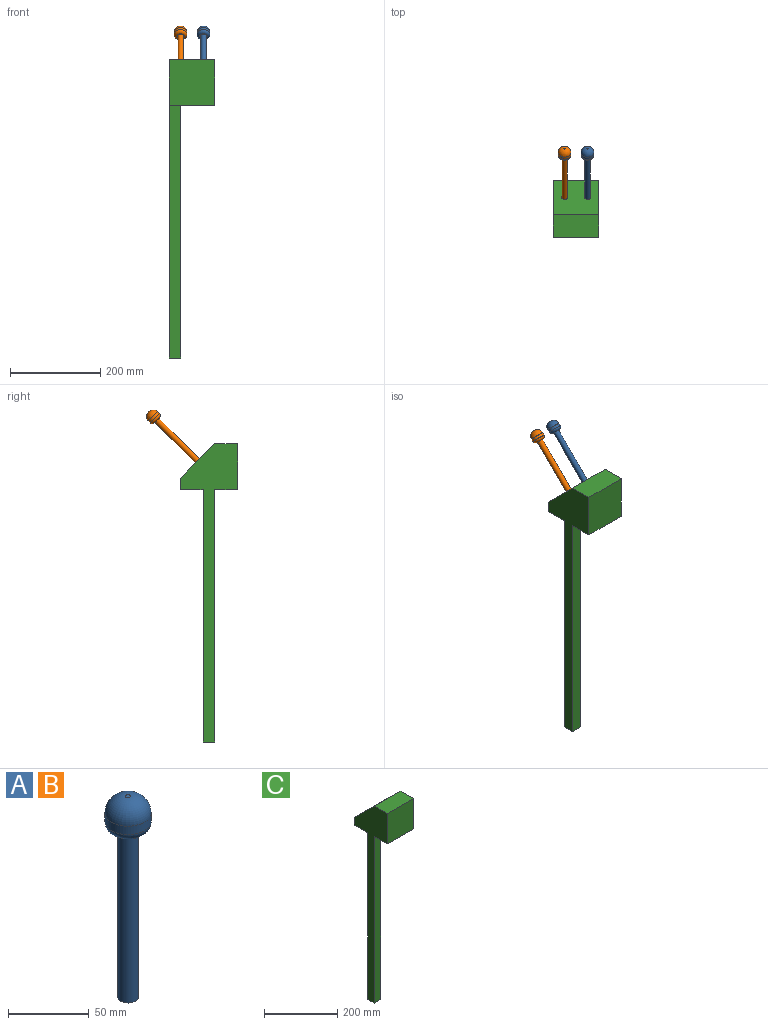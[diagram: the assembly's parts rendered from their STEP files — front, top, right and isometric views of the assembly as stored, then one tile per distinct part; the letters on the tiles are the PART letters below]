
ASSEMBLY  parts=3 mates=2
PART A: 7 faces, bbox 30.9x30.9x152.4 mm
  f0: cylinder r=6.35mm len=127mm, axis (0,0,-1), area 5067.1mm2, adj f1,f3
  f1: plane 12.7x12.7mm, normal (0,0,-1), area 126.7mm2, adj f0
  f2: cylinder r=14.29mm len=28.58mm, axis (0,0,-1), area 570mm2, adj f5,f6
  f3: plane 15.88x15.88mm, normal (0,0,-1), area 71.3mm2, adj f0,f6
  f4: plane 3.18x3.18mm, normal (0,0,1), area 7.9mm2, adj f5
  f5: torus R=1.59mm, axis (0,0,1), area 1212.4mm2, adj f2,f4
  f6: torus R=7.94mm, axis (0,0,1), area 750.8mm2, adj f2,f3
PART B: same geometry as A
PART C: 11 faces, bbox 101.6x127x660.4 mm
  f0: plane 558.8x25.4mm, normal (0,-1,0), area 14193.5mm2, adj f1,f3,f5,f9
  f1: plane 558.8x25.4mm, normal (1,0,0), area 14193.5mm2, adj f0,f2,f5,f9
  f2: plane 558.8x25.4mm, normal (0,1,0), area 14193.5mm2, adj f1,f3,f5,f9
  f3: plane 660.4x127mm, normal (-1,0,0), area 24193.5mm2, adj f0,f2,f4,f5,f6,f8,f9,f10
  f4: plane 101.6x50.8mm, normal (0,0,1), area 5161.3mm2, adj f3,f6,f7,f10
  f5: plane 25.4x25.4mm, normal (0,0,-1), area 645.2mm2, adj f0,f1,f2,f3
  f6: plane 101.6x101.6mm, normal (0,-1,0), area 10322.6mm2, adj f3,f4,f7,f9
  f7: plane 127x101.6mm, normal (1,0,0), area 10000mm2, adj f4,f6,f8,f9,f10
  f8: plane 101.6x25.4mm, normal (0,1,0), area 2580.6mm2, adj f3,f7,f9,f10
  f9: plane 127x101.6mm, normal (0,0,-1), area 12258mm2, adj f0,f1,f2,f3,f6,f7,f8
  f10: plane 101.6x76.2mm, normal (0,0.71,0.71), area 10948.7mm2, adj f3,f4,f7,f8
PLACE A rot(axis=(-1,0,0),45deg) t=(63.5,25.4,419.1)mm
PLACE B rot(axis=(-1,0,0),45deg) t=(12.7,25.4,419.1)mm
PLACE C at identity
MATE fastened B.f0 <-> C.f10  axis (0,-0.71,-0.71) through (12.7,25.4,419.1)mm
MATE fastened A.f0 <-> C.f10  axis (0,-0.71,-0.71) through (63.5,25.4,419.1)mm
